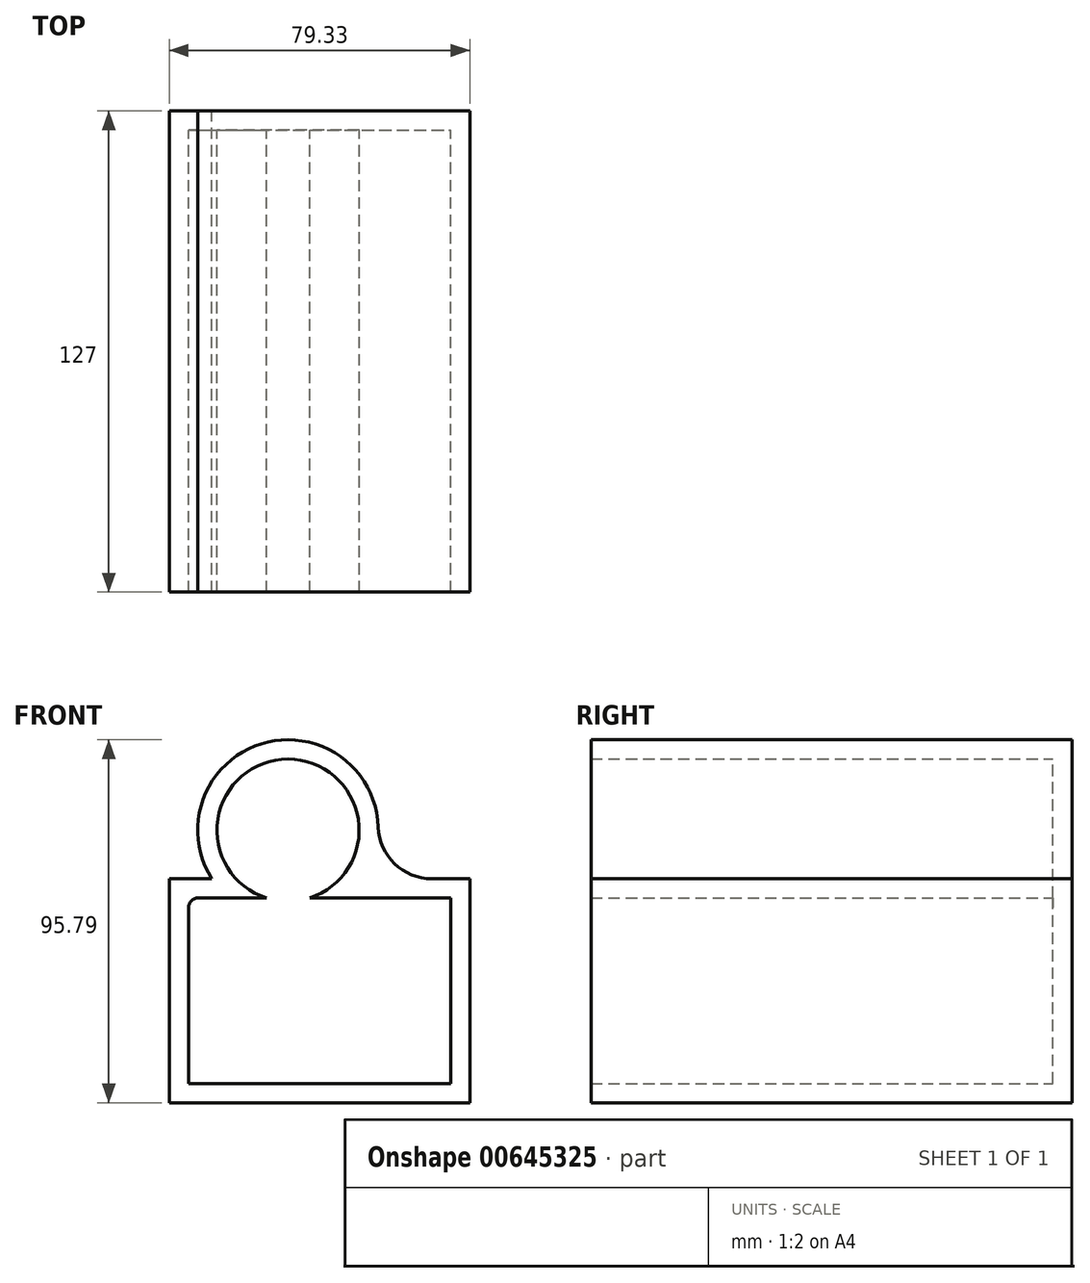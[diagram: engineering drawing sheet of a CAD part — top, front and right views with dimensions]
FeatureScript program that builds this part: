
annotation { "Feature Type Name" : "Feature", "Feature Type Description" : "" }
export const myFeature = defineFeature(function(context is Context, id is Id, definition is map)
    precondition{}
    {
        {
            var Q0;
            Q0=qCreatedBy(makeId("Front.planeOp"),FACE);
            var sketch = newSketch(context, id + "F0", { "sketchPlane" : qUnion([Q0])});
            skLineSegment(sketch, "E0.bottom", {"start": v(0, 0) * mm, "end": v(79.33, 0) * mm});
            skLineSegment(sketch, "E0.top", {"start": v(0, 59.12) * mm, "end": v(11.2, 59.12) * mm});
            skLineSegment(sketch, "E0.left", {"start": v(0, 0) * mm, "end": v(0, 59.12) * mm});
            skLineSegment(sketch, "E0.right", {"start": v(79.33, 0) * mm, "end": v(79.33, 59.12) * mm});
            skArc(sketch, "E1", {"start": v(51.46, 59.12) * mm, "mid": v(31.33, 95.8) * mm, "end": v(11.2, 59.12) * mm});
            skLineSegment(sketch, "E2", {"start": v(51.46, 59.12) * mm, "end": v(79.33, 59.12) * mm});
            skSolve(sketch);
        }
        {
            var Q0;
            Q0=makeQuery(id+"F0.imprint","IMPRINT",FACE,{"disambiguationData":[TD([[makeQuery(id+"F0.imprint","IMPRINT",EDGE,{"derivedFrom":sQuery(id+"F0.wireOp",EDGE,"E0.bottom")}),1.0]])]});
            extrude(context, id + "F1", {"entities" : qUnion([Q0]), "depth" : 127 * mm, "offsetDistance" : 25.4 * mm});
        }
        {
            var Q0;
            Q0=makeQuery(id+"F1.opExtrude","CAP_FACE",FACE,{"disambiguationData":[OSD([sQuery(id+"F0.wireOp",EDGE,"E0.bottom"),sQuery(id+"F0.wireOp",EDGE,"E0.top"),sQuery(id+"F0.wireOp",EDGE,"E0.left"),sQuery(id+"F0.wireOp",EDGE,"E0.right"),sQuery(id+"F0.wireOp",EDGE,"E1"),sQuery(id+"F0.wireOp",EDGE,"E2")])],"isStart":false});
            shell(context, id + "F2", {"entities" : qUnion([Q0]), "thickness" : 5.08 * mm});
        }
        {
            var Q0;
            Q0=makeQuery(id+"F2.opShell","OFFSET_EDGE",EDGE,{"disambiguationData":[OSD([sQuery(id+"F0.wireOp",EDGE,"E0.top"),sQuery(id+"F0.wireOp",EDGE,"E0.left")])]});
            fillet(context, id + "F3", {"entities" : qUnion([Q0]), "radius" : 2.54 * mm, "tangentPropagation" : true, "allowEdgeOverflow" : false});
        }
        {
            var Q0;
            Q0=makeQuery(id+"F1.opExtrude","SWEPT_EDGE",EDGE,{"disambiguationData":[OSD([sQuery(id+"F0.wireOp",EDGE,"E1"),sQuery(id+"F0.wireOp",EDGE,"E2")])]});
            fillet(context, id + "F4", {"entities" : qUnion([Q0]), "radius" : 14.13 * mm, "tangentPropagation" : true, "allowEdgeOverflow" : false});
        }
    });
